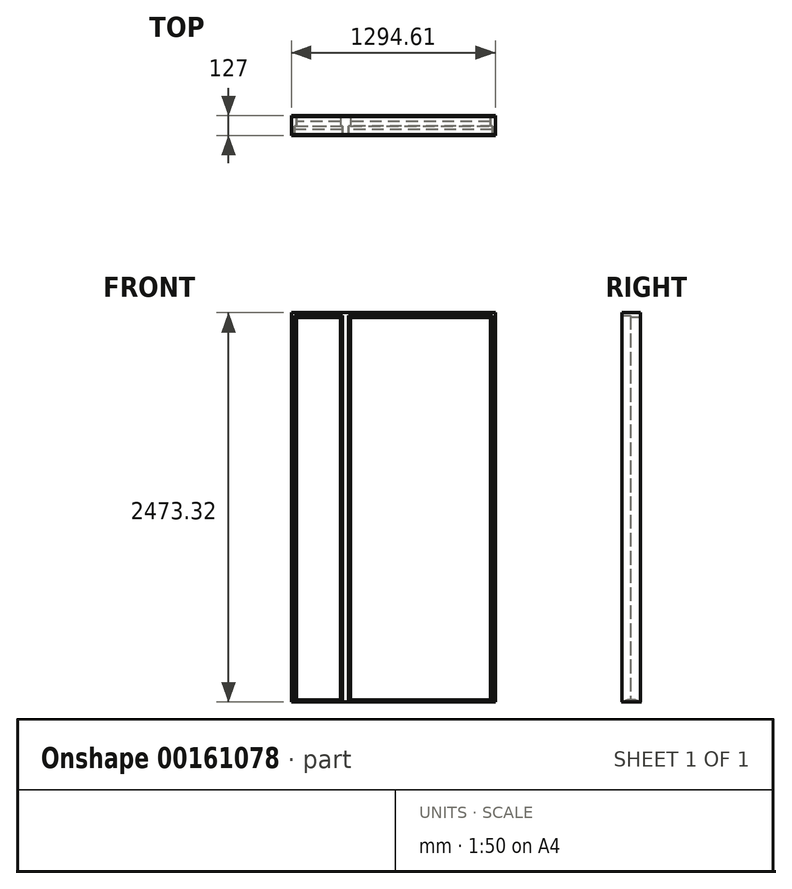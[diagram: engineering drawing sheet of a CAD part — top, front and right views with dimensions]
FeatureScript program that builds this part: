
annotation { "Feature Type Name" : "Feature", "Feature Type Description" : "" }
export const myFeature = defineFeature(function(context is Context, id is Id, definition is map)
    precondition{}
    {
        {
            var Q0;
            Q0=qCreatedBy(makeId("Front.planeOp"),FACE);
            cPlane(context, id + "F0", {"entities" : qUnion([Q0]), "cplaneType" : CPlaneType.OFFSET, "offset" : 3.17 * mm, "oppositeDirection" : true, "width" : 152.4 * mm, "height" : 152.4 * mm});
        }
        {
            var Q0;
            Q0=qCreatedBy(makeId("Front.planeOp"),FACE);
            var sketch = newSketch(context, id + "F1", { "sketchPlane" : qUnion([Q0])});
            skLineSegment(sketch, "E0.bottom", {"start": v(0, 0) * mm, "end": v(19.05, 0) * mm});
            skLineSegment(sketch, "E0.top", {"start": v(0, 2454.28) * mm, "end": v(19.05, 2454.28) * mm});
            skLineSegment(sketch, "E0.left", {"start": v(0, 0) * mm, "end": v(0, 2454.28) * mm});
            skLineSegment(sketch, "E0.right", {"start": v(19.05, 0) * mm, "end": v(19.05, 2454.28) * mm});
            skLineSegment(sketch, "E1.bottom", {"start": v(31.75, 2441.58) * mm, "end": v(19.05, 2441.58) * mm});
            skLineSegment(sketch, "E1.top", {"start": v(31.75, 0) * mm, "end": v(19.05, 0) * mm});
            skLineSegment(sketch, "E1.left", {"start": v(31.75, 2441.58) * mm, "end": v(31.75, 0) * mm});
            skLineSegment(sketch, "E1.right", {"start": v(19.05, 2441.58) * mm, "end": v(19.05, 0) * mm});
            skLineSegment(sketch, "E2.left", {"start": v(0, 2454.28) * mm, "end": v(0, 2473.33) * mm});
            skPoint(sketch, "E3.oppositeSnap0", {"position": v(9.53, 0) * mm});
            skLineSegment(sketch, "E4.left", {"start": v(19.05, 2454.28) * mm, "end": v(19.05, 2441.58) * mm});
            skLineSegment(sketch, "E5.bottom", {"start": v(342.9, 2454.28) * mm, "end": v(323.85, 2454.28) * mm});
            skLineSegment(sketch, "E5.top", {"start": v(342.9, 0) * mm, "end": v(323.85, 0) * mm});
            skLineSegment(sketch, "E5.left", {"start": v(342.9, 2454.28) * mm, "end": v(342.9, 0) * mm});
            skLineSegment(sketch, "E5.right", {"start": v(323.85, 2454.28) * mm, "end": v(323.85, 0) * mm});
            skLineSegment(sketch, "E6.bottom", {"start": v(323.85, 0) * mm, "end": v(311.15, 0) * mm});
            skLineSegment(sketch, "E6.top", {"start": v(323.85, 2441.58) * mm, "end": v(311.15, 2441.58) * mm});
            skLineSegment(sketch, "E6.left", {"start": v(323.85, 0) * mm, "end": v(323.85, 2441.58) * mm});
            skLineSegment(sketch, "E6.right", {"start": v(311.15, 0) * mm, "end": v(311.15, 2441.58) * mm});
            skLineSegment(sketch, "E7.bottom", {"start": v(342.9, 2454.28) * mm, "end": v(361.95, 2454.28) * mm});
            skLineSegment(sketch, "E7.top", {"start": v(342.9, 0) * mm, "end": v(361.95, 0) * mm});
            skLineSegment(sketch, "E7.right", {"start": v(361.95, 2454.28) * mm, "end": v(361.95, 0) * mm});
            skLineSegment(sketch, "E8.bottom", {"start": v(361.95, 0) * mm, "end": v(374.65, 0) * mm});
            skLineSegment(sketch, "E8.top", {"start": v(361.95, 2441.58) * mm, "end": v(374.65, 2441.58) * mm});
            skLineSegment(sketch, "E8.left", {"start": v(361.95, 0) * mm, "end": v(361.95, 2441.58) * mm});
            skLineSegment(sketch, "E8.right", {"start": v(374.65, 0) * mm, "end": v(374.65, 2441.58) * mm});
            skLineSegment(sketch, "E9.bottom", {"start": v(1294.6, 2454.28) * mm, "end": v(1275.56, 2454.28) * mm});
            skLineSegment(sketch, "E9.top", {"start": v(1294.6, 0) * mm, "end": v(1275.56, 0) * mm});
            skLineSegment(sketch, "E9.left", {"start": v(1294.6, 2454.28) * mm, "end": v(1294.6, 0) * mm});
            skLineSegment(sketch, "E9.right", {"start": v(1275.56, 2454.28) * mm, "end": v(1275.56, 0) * mm});
            skLineSegment(sketch, "E10.left", {"start": v(1294.6, 0) * mm, "end": v(1294.6, 2454.28) * mm});
            skLineSegment(sketch, "E11.bottom", {"start": v(1275.56, 2441.58) * mm, "end": v(1262.86, 2441.58) * mm});
            skLineSegment(sketch, "E11.top", {"start": v(1275.56, 0) * mm, "end": v(1262.86, 0) * mm});
            skLineSegment(sketch, "E11.left", {"start": v(1275.56, 2441.58) * mm, "end": v(1275.56, 0) * mm});
            skLineSegment(sketch, "E11.right", {"start": v(1262.86, 2441.58) * mm, "end": v(1262.86, 0) * mm});
            skLineSegment(sketch, "E12.bottom", {"start": v(19.05, 2454.28) * mm, "end": v(323.85, 2454.28) * mm});
            skLineSegment(sketch, "E12.top", {"start": v(19.05, 2441.58) * mm, "end": v(323.85, 2441.58) * mm});
            skLineSegment(sketch, "E12.right", {"start": v(323.85, 2454.28) * mm, "end": v(323.85, 2441.58) * mm});
            skLineSegment(sketch, "E13.bottom", {"start": v(361.95, 2454.28) * mm, "end": v(1275.56, 2454.28) * mm});
            skLineSegment(sketch, "E13.top", {"start": v(361.95, 2441.58) * mm, "end": v(1275.56, 2441.58) * mm});
            skLineSegment(sketch, "E13.left", {"start": v(361.95, 2454.28) * mm, "end": v(361.95, 2441.58) * mm});
            skLineSegment(sketch, "E13.right", {"start": v(1275.56, 2454.28) * mm, "end": v(1275.56, 2441.58) * mm});
            skLineSegment(sketch, "E14", {"start": v(0, 2473.33) * mm, "end": v(1294.6, 2473.33) * mm});
            skLineSegment(sketch, "E15", {"start": v(1294.6, 2473.33) * mm, "end": v(1294.6, 2454.28) * mm});
            skSolve(sketch);
        }
        {
            var Q0;
            Q0=qCreatedBy(id+"F0.planeOp",FACE);
            var sketch = newSketch(context, id + "F2", { "sketchPlane" : qUnion([Q0])});
            skLineSegment(sketch, "E16.0", {"start": v(0, 0) * mm, "end": v(0, 2454.28) * mm});
            skLineSegment(sketch, "E17.0", {"start": v(0, 0) * mm, "end": v(19.05, 0) * mm});
            skLineSegment(sketch, "E18.0", {"start": v(31.75, 0) * mm, "end": v(19.05, 0) * mm});
            skLineSegment(sketch, "E19.0", {"start": v(31.75, 2441.58) * mm, "end": v(31.75, 0) * mm});
            skLineSegment(sketch, "E20.0", {"start": v(19.05, 2441.58) * mm, "end": v(323.85, 2441.58) * mm});
            skLineSegment(sketch, "E21.0", {"start": v(311.15, 0) * mm, "end": v(311.15, 2441.58) * mm});
            skLineSegment(sketch, "E22.0", {"start": v(0, 2454.28) * mm, "end": v(0, 2473.33) * mm});
            skLineSegment(sketch, "E23.0", {"start": v(361.95, 2441.58) * mm, "end": v(1275.56, 2441.58) * mm});
            skLineSegment(sketch, "E24.0", {"start": v(374.65, 0) * mm, "end": v(374.65, 2441.58) * mm});
            skLineSegment(sketch, "E25.0", {"start": v(1262.86, 2441.58) * mm, "end": v(1262.86, 0) * mm});
            skLineSegment(sketch, "E26.0", {"start": v(323.85, 0) * mm, "end": v(311.15, 0) * mm});
            skLineSegment(sketch, "E27.0", {"start": v(342.9, 0) * mm, "end": v(323.85, 0) * mm});
            skLineSegment(sketch, "E28.0", {"start": v(342.9, 0) * mm, "end": v(361.95, 0) * mm});
            skLineSegment(sketch, "E29.0", {"start": v(361.95, 0) * mm, "end": v(374.65, 0) * mm});
            skLineSegment(sketch, "E30.0", {"start": v(1275.56, 0) * mm, "end": v(1262.86, 0) * mm});
            skLineSegment(sketch, "E31.0", {"start": v(1294.6, 0) * mm, "end": v(1275.56, 0) * mm});
            skLineSegment(sketch, "E32.0", {"start": v(0, 2473.33) * mm, "end": v(1294.6, 2473.33) * mm});
            skLineSegment(sketch, "E33.0", {"start": v(1294.6, 2473.33) * mm, "end": v(1294.6, 2454.28) * mm});
            skLineSegment(sketch, "E34.0", {"start": v(1294.6, 0) * mm, "end": v(1294.6, 2454.28) * mm});
            skSolve(sketch);
        }
        {
            var Q0;
            Q0=qSketchRegion(id+"F2",true);
            extrude(context, id + "F3", {"entities" : qUnion([Q0]), "oppositeDirection" : true, "depth" : 61.9 * mm});
        }
        {
            var Q0;
            Q0=qCreatedBy(makeId("Front.planeOp"),FACE);
            var sketch = newSketch(context, id + "F4", { "sketchPlane" : qUnion([Q0])});
            skLineSegment(sketch, "E35.0", {"start": v(0, 0) * mm, "end": v(19.05, 0) * mm});
            skLineSegment(sketch, "E36.0", {"start": v(19.05, 2441.58) * mm, "end": v(19.05, 0) * mm});
            skLineSegment(sketch, "E37.0", {"start": v(0, 0) * mm, "end": v(0, 2454.28) * mm});
            skLineSegment(sketch, "E38.0", {"start": v(0, 2454.28) * mm, "end": v(0, 2473.33) * mm});
            skLineSegment(sketch, "E39.0", {"start": v(19.05, 2454.28) * mm, "end": v(19.05, 2441.58) * mm});
            skLineSegment(sketch, "E40.0", {"start": v(19.05, 2454.28) * mm, "end": v(323.85, 2454.28) * mm});
            skLineSegment(sketch, "E41.0", {"start": v(323.85, 2454.28) * mm, "end": v(323.85, 0) * mm});
            skLineSegment(sketch, "E42.0", {"start": v(361.95, 2454.28) * mm, "end": v(361.95, 0) * mm});
            skLineSegment(sketch, "E43.0", {"start": v(342.9, 0) * mm, "end": v(323.85, 0) * mm});
            skLineSegment(sketch, "E44.0", {"start": v(342.9, 0) * mm, "end": v(361.95, 0) * mm});
            skLineSegment(sketch, "E45.0", {"start": v(1275.56, 2454.28) * mm, "end": v(1275.56, 2441.58) * mm});
            skLineSegment(sketch, "E46.0", {"start": v(1275.56, 2441.58) * mm, "end": v(1275.56, 0) * mm});
            skLineSegment(sketch, "E47", {"start": v(1275.56, 2454.28) * mm, "end": v(361.95, 2454.28) * mm});
            skLineSegment(sketch, "E48.0", {"start": v(1294.6, 0) * mm, "end": v(1275.56, 0) * mm});
            skLineSegment(sketch, "E49.0", {"start": v(0, 2473.33) * mm, "end": v(1294.6, 2473.33) * mm});
            skLineSegment(sketch, "E50.0", {"start": v(1294.6, 2473.33) * mm, "end": v(1294.6, 2454.28) * mm});
            skLineSegment(sketch, "E51.0", {"start": v(1294.6, 0) * mm, "end": v(1294.6, 2454.28) * mm});
            skSolve(sketch);
        }
        {
            var Q0;
            Q0=qSketchRegion(id+"F4",true);
            extrude(context, id + "F5", {"entities" : qUnion([Q0]), "operationType" : NewBodyOperationType.ADD, "depth" : 50.8 * mm, "hasSecondDirection" : true, "secondDirectionOppositeDirection" : true, "secondDirectionDepth" : 3.17 * mm});
        }
        {
            var Q0;
            Q0=qCreatedBy(makeId("Right.planeOp"),FACE);
            var sketch = newSketch(context, id + "F6", { "sketchPlane" : qUnion([Q0])});
            skLineSegment(sketch, "E52", {"start": v(-18.26, 12.7) * mm, "end": v(32.54, 12.7) * mm});
            skLineSegment(sketch, "E53", {"start": v(-56.36, 0) * mm, "end": v(-18.26, 12.7) * mm});
            skLineSegment(sketch, "E54", {"start": v(32.54, 12.7) * mm, "end": v(70.64, 0) * mm});
            skLineSegment(sketch, "E55.0", {"start": v(65.09, 0) * mm, "end": v(-50.8, 0) * mm});
            skLineSegment(sketch, "E56", {"start": v(7.14, 0) * mm, "end": v(70.64, 0) * mm});
            skLineSegment(sketch, "E57", {"start": v(7.14, 0) * mm, "end": v(-56.36, 0) * mm});
            skSolve(sketch);
        }
        {
            var Q0;
            Q0=qSketchRegion(id+"F6",true);
            var Q1;
            Q1=makeQuery(id+"F5.boolean.opBoolean","MERGE",FACE,{"derivedFrom":[makeQuery(id+"F3.opExtrude","SWEPT_FACE",FACE,{"disambiguationData":[OSD([sQuery(id+"F2.wireOp",EDGE,"E33.0"),sQuery(id+"F2.wireOp",EDGE,"E34.0")])]}),makeQuery(id+"F5.opExtrude","SWEPT_FACE",FACE,{"disambiguationData":[OSD([sQuery(id+"F4.wireOp",EDGE,"E50.0"),sQuery(id+"F4.wireOp",EDGE,"E51.0")])]})]});
            extrude(context, id + "F7", {"entities" : qUnion([Q0]), "operationType" : NewBodyOperationType.ADD, "endBound" : BoundingType.UP_TO_SURFACE, "endBoundEntityFace" : qUnion([Q1]), "depth" : 25.4 * mm});
        }
    });
